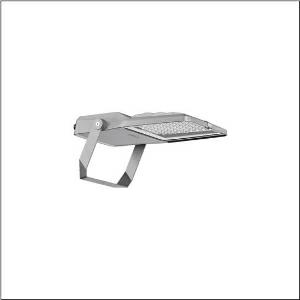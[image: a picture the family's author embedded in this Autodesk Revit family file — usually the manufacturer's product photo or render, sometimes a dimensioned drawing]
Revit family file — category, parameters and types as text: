
# Revit family: floodlight_fl_21_iq_mini___pl33t_5xa7772d1f1a_784a
name_source: partatom
category: Lighting Fixtures
units: mm (PartAtom-declared; Revit-internal decimal feet)

## family parameters
Cut with Voids When Loaded = No
Host = Face
Light Source = No
Part Type = Normal
Room Calculation Point = No
Round Connector Dimension = Use Diameter
Shared = No

## types (1)
- --- (1 x LED, 14590 lm, 143 W, 2200K)
    Apparent Load = 143 VA
    CIE Flux Codes = 26 75 99 100 100
    Color Rendering = 70
    Color Temperature = 2200K
    Default Elevation = 1800 mm
    Description = Floodlight FL 21 iQ mini, floodlight, primary light control with lens, of PMMA, primary optical cover: protective disc, of toughened safety glass, transparent, light distribution: PL33T, light emission: direct distribution, installation type: surface-mounted, LED, High Power LED, rated luminous flux: 14.590lm, luminous efficacy: 102lm/W, light colour: 722, colour temperature: 2200K, control gear: iQ Street-Remote/DALI, control: Street-Remote, Auto-Match, Temp-Guard, Night-Set, Smart-Wire, Desk-Remote (wireless, voltage-free reading and setting of iQ features in the workshop via application-optimized NFC function/RFID function), optimised constant luminous flux control (CLO 2.0), with terminal, 6-pole, mains connection: 220..240V, AC, 50/60Hz, start of lifetime: 143W, end of service life: 152W, reduction: 61W, luminaire housing, of diecast aluminium, powder-coated, Siteco® metallic grey (DB 702S), corrosivity category C5 mid according to DIN EN ISO 12944, suitable for swimming pools, chlorine-resistant, sealing non-destructively replaceable, mounting bracket, of steel, galvanised, powder-coated, Siteco® metallic grey (DB 702S), protection rating (complete): IP66, insulation class (complete): insulation class II (safety insulation), certification: CE, ENEC, VDE, protection symbol: D, impact resistance: IK08, permissible operating ambient temperature: -40..+40°C, permissible operating ambient temperature for outdoor applications: -40..+50°C, standard: DIN EN 12944, LABS conformity tested according to VDMA 24364:2018-05, packaging unit: 1 piece

Light Distribution: PL33T
    Height = 70 mm
    Lamp = 1 x LED
    Lamp Light Flux = 14590 lm
    Lamp Power = 143 W
    Lamp count = 1
    Length = 485 mm
    Luminous efficacy = 102 lm/W
    Manufacturer = Siteco
    ModVariant = No
    Model = 5XA7772D1F1A
    Number of Poles = 1
    OnlyDefault = Yes
    Power Factor = 1
    Product Name = Floodlight FL 21 iQ mini | PL33T
    Product group = floodlight | pylon annexe
    ProductGroupID = 6200
    Protection Class = Protection class II
    Protection Degree = IP 66
    RLX_Detail_Level = 1
    RLX_Emergency_Light_Flux = 0 lm
    RLX_Emergency_Type = 0
    RLX_Emergency_Type_DB = No
    RlxData = <blob elided: 96501 chars, md5=a292859b>
    Socket = socket
    Standby Power = 0 W
    System Light Flux = 14590 lm
    System Power = 143 W
    Type Comments = factory setting: luminous flux: 100 % | dim-lin: 254 | 730 mA
    Type Image = l_1006845.jpg
    URL = http://relux.com
    VarID = @adj_149046
    Voltage = 0 V
    Weight = 0.00 kg
    Width = 337 mm

## geometry (parser evidence)
native form markers: Blend x4, Sweep x12
no freeform markers — native parametric forms only
